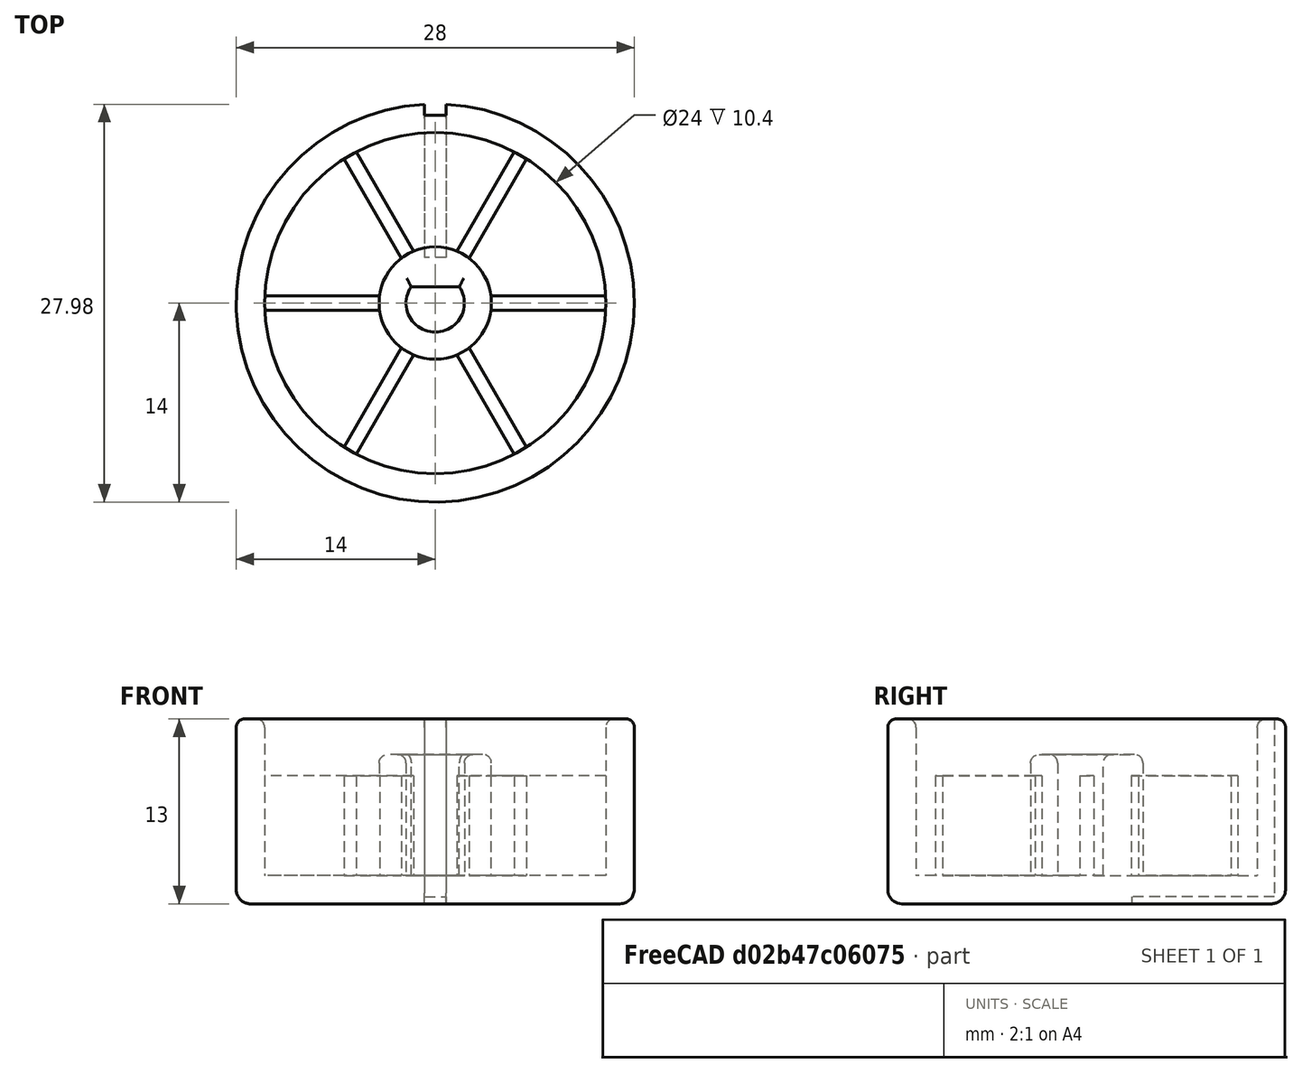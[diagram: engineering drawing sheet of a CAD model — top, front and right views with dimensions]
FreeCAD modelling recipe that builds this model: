
FCSTD DOCUMENT  (FreeCAD 1.0R39109 (Git))
Label: fan_regulator_knob
License: All rights reserved
LicenseURL: http://www.ohwr.org/attachments/2388/cern_ohl_v_1_2.txt
objects: Sketcher::SketchObject×6, PartDesign::Pad×4, PartDesign::Pocket×2, PartDesign::Fillet×2, Mesh::Feature×1, Spreadsheet::Sheet×1, PartDesign::PolarPattern×1, PartDesign::Body×1
note: 39 computed .brp shape members not serialized (recipe doc carries the construction recipe); baked Part::Feature solids carry a one-line shape summary decoded from their .brp

FEATURE [Mesh::Feature] Regulator_Knob
FEATURE [Spreadsheet::Sheet] Spreadsheet
  cells = A1='dia_shaft; B1(dia_shaft)=3.9; C1=3.9; D1=6; A2='D_length; B2(D_length)=3; C2=3; D2=5; A3='dia_outer; B3(dia_outer)=28; A4='dia_nozzle; B4(dia_nozzle)=0.4
FEATURE [Sketcher::SketchObject] Sketch001
  ArcFitTolerance = 1e-06
  AttachmentSupport = -> [XY_Plane]
  FullyConstrained = true
  MakeInternals = false
  MapMode = 5
  expr: Constraints[1] = Spreadsheet.dia_outer
  sketch-geometry (1):
    g0: Circle CenterX=0 CenterY=0 CenterZ=0 NormalX=0 NormalY=0 NormalZ=1 AngleXU=0 Radius=14
  constraints (2):
    c: Coincident(g0,g-1)
    c: Diameter(g0) = 28
FEATURE [PartDesign::Pad] Pad
  Direction = (0,0,1)
  Length = 2
  Length2 = 10
  Profile = -> Sketch001
  ReferenceAxis = -> Sketch001 [N_Axis]
  Refine = true
  Suppressed = false
  Type = 0
FEATURE [Sketcher::SketchObject] Sketch
  ArcFitTolerance = 1e-06
  AttachmentSupport = -> [Pad]
  ExternalGeometry = -> [Pad]
  FullyConstrained = true
  MakeInternals = false
  MapMode = 5
  Placement = pos=(0,0,2) rot=(0,0,1;0rad)
  expr: Constraints[0] = Spreadsheet.dia_shaft + Spreadsheet.dia_nozzle / 2
  expr: Constraints[11] = Spreadsheet.dia_shaft + 4
  expr: Constraints[14] = Spreadsheet.dia_outer
  expr: Constraints[15] = Spreadsheet.dia_outer - 4
  expr: Constraints[5] = Spreadsheet.D_length + Spreadsheet.dia_nozzle / 2
  sketch-geometry (6):
    g0: ArcOfCircle CenterX=0 CenterY=0 CenterZ=0 NormalX=0 NormalY=0 NormalZ=1 AngleXU=0 Radius=2.05 StartAngle=2.54603 EndAngle=6.87875
    g1: LineSegment StartX=-1.69706 StartY=1.15 StartZ=0 EndX=1.69706 EndY=1.15 EndZ=0
    g2: LineSegment [constr] StartX=0 StartY=1.15 StartZ=0 EndX=0 EndY=-2.05 EndZ=0
    g3: Circle CenterX=0 CenterY=0 CenterZ=0 NormalX=0 NormalY=0 NormalZ=1 AngleXU=0 Radius=3.95
    g4: Circle CenterX=0 CenterY=0 CenterZ=0 NormalX=0 NormalY=0 NormalZ=1 AngleXU=0 Radius=14
    g5: Circle CenterX=0 CenterY=0 CenterZ=0 NormalX=0 NormalY=0 NormalZ=1 AngleXU=0 Radius=12
  constraints (16):
    c: Diameter(g0) = 4.1
    c: Coincident(g0,g-1)
    c: Horizontal(g1)
    c: Coincident(g0,g1)
    c: Coincident(g0,g1)
    c: DistanceY(g2,g2) = 3.2
    c: PointOnObject(g2,g1)
    c: PointOnObject(g2,g0)
    c: Vertical(g2)
    c: PointOnObject(g2,g-2)
    c: Coincident(g3,g0)
    c: Diameter(g3) = 7.9
    c: Coincident(g4,g0)
    c: Coincident(g5,g0)
    c: Diameter(g4) = 28
    c: Diameter(g5) = 24
FEATURE [PartDesign::Pad] Pad001
  BaseFeature = -> Pad
  Direction = (0,0,1)
  Length = 8.5
  Length2 = 10
  Profile = -> Sketch
  ReferenceAxis = -> Sketch [N_Axis]
  Refine = true
  Suppressed = false
  Type = 0
FEATURE [Sketcher::SketchObject] Sketch002
  ArcFitTolerance = 1e-06
  AttachmentSupport = -> [Pad001]
  ExternalGeometry = -> [Pad001]
  FullyConstrained = true
  MakeInternals = false
  MapMode = 5
  Placement = pos=(0,0,10.5) rot=(0,0,1;0rad)
  sketch-geometry (2):
    g0: Circle CenterX=0 CenterY=0 CenterZ=0 NormalX=0 NormalY=0 NormalZ=1 AngleXU=0 Radius=14
    g1: Circle CenterX=0 CenterY=0 CenterZ=0 NormalX=0 NormalY=0 NormalZ=1 AngleXU=0 Radius=12
  constraints (4):
    c: Coincident(g0,g-1)
    c: Coincident(g1,g0)
    c: Equal(g-3,g0)
    c: Equal(g1,g-4)
FEATURE [PartDesign::Pad] Pad002
  BaseFeature = -> Pad001
  Direction = (0,0,1)
  Length = 2.5
  Length2 = 10
  Profile = -> Sketch002
  ReferenceAxis = -> Sketch002 [N_Axis]
  Refine = true
  Suppressed = false
  Type = 0
FEATURE [Sketcher::SketchObject] Sketch003
  ArcFitTolerance = 1e-06
  AttachmentSupport = -> [Pad002]
  ExternalGeometry = -> [Pad002]
  FullyConstrained = true
  MakeInternals = false
  MapMode = 5
  Placement = pos=(0,0,2) rot=(0,0,1;0rad)
  sketch-geometry (4):
    g0: LineSegment StartX=-12 StartY=0.5 StartZ=0 EndX=-12 EndY=-0.5 EndZ=0
    g1: LineSegment StartX=-12 StartY=-0.5 StartZ=0 EndX=-3.54996 EndY=-0.5 EndZ=0
    g2: LineSegment StartX=-3.54996 StartY=-0.5 StartZ=0 EndX=-3.54996 EndY=0.5 EndZ=0
    g3: LineSegment StartX=-3.54996 StartY=0.5 StartZ=0 EndX=-12 EndY=0.5 EndZ=0
  constraints (11):
    c: Coincident(g0,g1)
    c: Coincident(g1,g2)
    c: Coincident(g2,g3)
    c: Coincident(g3,g0)
    c: Vertical(g2)
    c: Horizontal(g1)
    c: Horizontal(g3)
    c: Symmetric(g0,g0,g-1)
    c: Tangent(g0,g-4)
    c: PointOnObject(g2,g-3)
    c: Distance(g0,g0) = 1
FEATURE [PartDesign::Pad] Pad003
  BaseFeature = -> Pad002
  Direction = (0,0,1)
  Length = 7
  Length2 = 10
  Profile = -> Sketch003
  ReferenceAxis = -> Sketch003 [N_Axis]
  Refine = true
  Suppressed = false
  Type = 0
FEATURE [PartDesign::PolarPattern] PolarPattern
  Angle = 360
  Axis = -> Sketch003 [N_Axis]
  BaseFeature = -> Pad003
  Mode = 0
  Occurrences = 6
  Offset = 120
  Originals = -> [Pad003]
  Refine = true
  Suppressed = false
  TransformMode = 0
FEATURE [Sketcher::SketchObject] Sketch004
  ArcFitTolerance = 1e-06
  AttachmentSupport = -> [PolarPattern]
  ExternalGeometry = -> [PolarPattern]
  FullyConstrained = true
  MakeInternals = false
  MapMode = 5
  Placement = pos=(0,0,13) rot=(0,0,1;0rad)
  sketch-geometry (4):
    g0: LineSegment StartX=-0.75 StartY=14 StartZ=0 EndX=-0.75 EndY=13.2 EndZ=0
    g1: LineSegment StartX=-0.75 StartY=13.2 StartZ=0 EndX=0.75 EndY=13.2 EndZ=0
    g2: LineSegment StartX=0.75 StartY=13.2 StartZ=0 EndX=0.75 EndY=14 EndZ=0
    g3: LineSegment StartX=0.75 StartY=14 StartZ=0 EndX=-0.75 EndY=14 EndZ=0
  constraints (11):
    c: Coincident(g0,g1)
    c: Coincident(g1,g2)
    c: Coincident(g2,g3)
    c: Coincident(g3,g0)
    c: Vertical(g0)
    c: Vertical(g2)
    c: Horizontal(g3)
    c: Tangent(g3,g-3)
    c: Symmetric(g1,g1,g-2)
    c: DistanceX(g1,g1) = 1.5
    c: DistanceY(g2,g2) = 0.8
FEATURE [PartDesign::Pocket] Pocket
  BaseFeature = -> PolarPattern
  Direction = (0,0,-1)
  Length = 5
  Length2 = 5
  Profile = -> Sketch004
  ReferenceAxis = -> Sketch004 [N_Axis]
  Refine = true
  Suppressed = false
  Type = 1
FEATURE [Sketcher::SketchObject] Sketch005
  ArcFitTolerance = 1e-06
  AttachmentSupport = -> [Pocket]
  ExternalGeometry = -> [Pocket]
  FullyConstrained = true
  MakeInternals = false
  MapMode = 5
  Placement = pos=(0,13.2,0) rot=(0,0.707107,0.707107;3.14159rad)
  sketch-geometry (4):
    g0: LineSegment StartX=-0.75 StartY=0 StartZ=0 EndX=0.75 EndY=0 EndZ=0
    g1: LineSegment StartX=0.75 StartY=0 StartZ=0 EndX=0.75 EndY=0.5 EndZ=0
    g2: LineSegment StartX=0.75 StartY=0.5 StartZ=0 EndX=-0.75 EndY=0.5 EndZ=0
    g3: LineSegment StartX=-0.75 StartY=0.5 StartZ=0 EndX=-0.75 EndY=0 EndZ=0
  constraints (11):
    c: Coincident(g0,g1)
    c: Coincident(g1,g2)
    c: Coincident(g2,g3)
    c: Coincident(g3,g0)
    c: Horizontal(g0)
    c: Horizontal(g2)
    c: Vertical(g1)
    c: Vertical(g3)
    c: Coincident(g0,g-5)
    c: PointOnObject(g1,g-4)
    c: Distance(g3,g3) = 0.5
FEATURE [PartDesign::Pocket] Pocket001
  BaseFeature = -> Pocket
  Direction = (0,-1,2e-16)
  Length = 10
  Length2 = 5
  Profile = -> Sketch005
  ReferenceAxis = -> Sketch005 [N_Axis]
  Refine = true
  Suppressed = false
  Type = 0
FEATURE [PartDesign::Fillet] Fillet
  Base = -> Pocket001 [Edge5,Edge4]
  BaseFeature = -> Pocket001
  Radius = 1
  Refine = true
  SupportTransform = false
  Suppressed = false
  UseAllEdges = false
FEATURE [PartDesign::Fillet] Fillet001
  Base = -> Fillet [Edge22,Edge23,Edge26,Edge108,Edge109,Edge110]
  BaseFeature = -> Fillet
  Radius = 0.6
  Refine = true
  SupportTransform = false
  Suppressed = false
  UseAllEdges = false
FEATURE [PartDesign::Body] Body
  AllowCompound = false
  Group = -> [Sketch,Sketch001,Pad,Pad001,Sketch002,Pad002,Sketch003,Pad003,PolarPattern,Sketch004,Pocket,Sketch005,Pocket001,Fillet,Fillet001]
  Origin = -> Origin
  Tip = -> Fillet001
